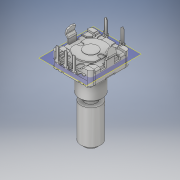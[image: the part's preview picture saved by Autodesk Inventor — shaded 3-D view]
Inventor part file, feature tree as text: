
AUTODESK INVENTOR PART (.ipt)
format: ipt  version: 2018 (Build 220112000, 112)  size: 515,072 bytes
history: native  units: mm
features: plane x1
ambient origin geometry x8: Origin, YZ Plane, XZ Plane, XY Plane, X Axis, Y Axis, Z Axis, Center Point
bodies: Volumenkörper1 (feature_tree)
feature tree (1):
  plane  "Arbeitsebene1"
